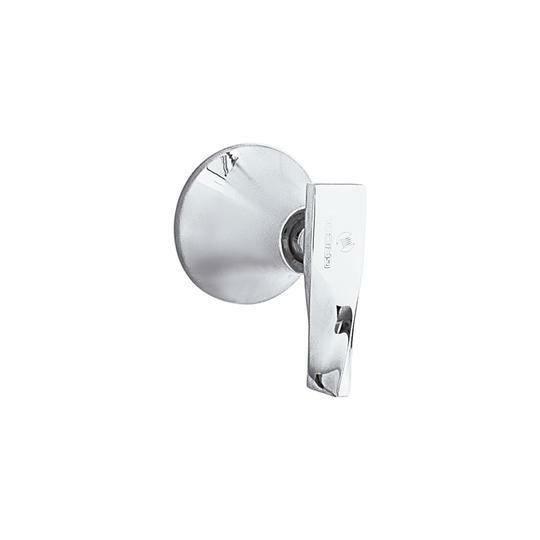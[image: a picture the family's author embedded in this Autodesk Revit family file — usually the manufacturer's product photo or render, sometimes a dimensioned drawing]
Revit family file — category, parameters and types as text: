
# Revit family: 01-2833-11-REGISTRO DUCHA PRISTINA
name_source: partatom
category: Aparatos sanitarios
revit_build: Autodesk Revit 2018 (Build: 20170223_1515(x64)
units: mm (PartAtom-declared; Revit-internal decimal feet)

## family parameters
Anfitrión = Cara
Compartido = No
Corte con vacíos al cargar = No
Cota de conector redondo = Diámetro de uso
Número OmniClass = 23.31.11.00
Punto de cálculo de habitación = No
Tipo de pieza = Normal

## types (1)
- 01-2833-11
    Alto = 60 mm  [stored 0.19685 ft]
    Ancho = 75.5 mm
    Conexión AC = Sí
    Conexión AF = Sí
    Conexión de residuos = No
    Conexión de ventilación = No
    Descripción = Registro ducha
    Elevación por defecto = 0 mm  [stored 0 ft]
    Fabricante = Gricol
    Imagen de tipo = <Ninguno>
    Link Ficha Tecnica = http://infotecnica.gricol.com
    Modelo = 01-2833-11
    Plastico ABS Cromado = Plastico ABS Cromado
    Product Name = REGISTRO DUCHA PRISTINA
    Profundidad = 77.5 mm
    URL = https://www.gricol.com

note: [stored X ft] marks values corroborated as IEEE doubles in the binary element streams (Revit-internal decimal feet)

## geometry (parser evidence)
native form markers: Blend x2, Sweep x5
no freeform markers — native parametric forms only
